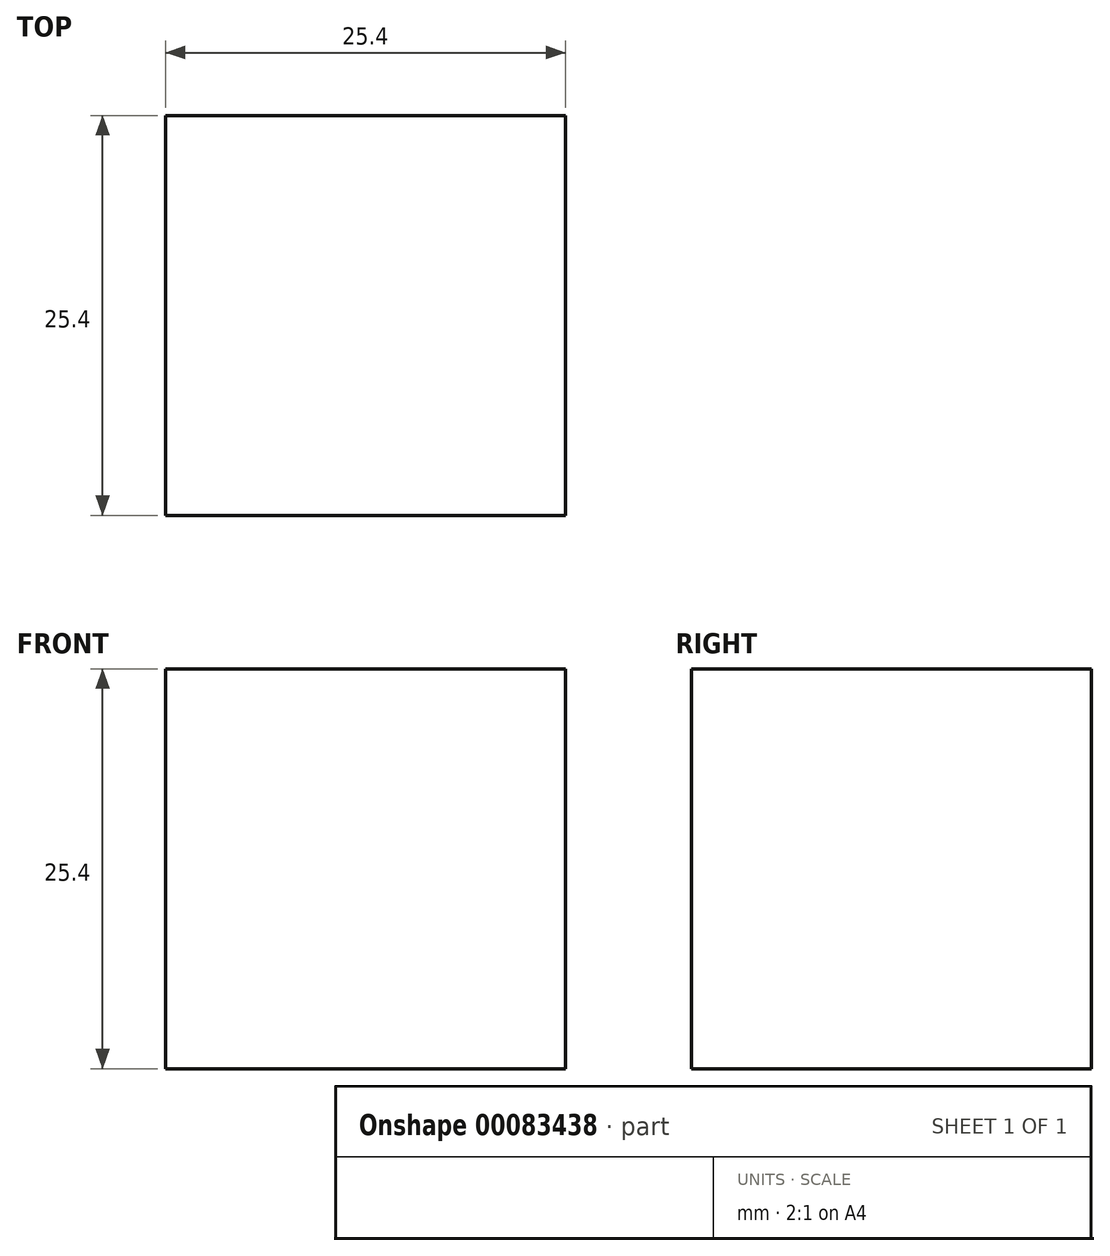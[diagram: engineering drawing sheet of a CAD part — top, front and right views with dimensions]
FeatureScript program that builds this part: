
annotation { "Feature Type Name" : "Feature", "Feature Type Description" : "" }
export const myFeature = defineFeature(function(context is Context, id is Id, definition is map)
    precondition{}
    {
        {
            var Q0;
            Q0=qCreatedBy(makeId("Top.planeOp"),FACE);
            var sketch = newSketch(context, id + "F0", { "sketchPlane" : qUnion([Q0])});
            skLineSegment(sketch, "E0.bottom", {"start": v(-12.7, 12.7) * mm, "end": v(12.7, 12.7) * mm});
            skLineSegment(sketch, "E0.top", {"start": v(-12.7, -12.7) * mm, "end": v(12.7, -12.7) * mm});
            skLineSegment(sketch, "E0.left", {"start": v(-12.7, 12.7) * mm, "end": v(-12.7, -12.7) * mm});
            skLineSegment(sketch, "E0.right", {"start": v(12.7, 12.7) * mm, "end": v(12.7, -12.7) * mm});
            skPoint(sketch, "E0.middle", {"position": v(0, 0) * mm});
            skSolve(sketch);
        }
        {
            var Q0;
            Q0 = qSketchRegion(id + "F0", true);
            extrude(context, id + "F1", {"entities" : qUnion([Q0]), "depth" : 25.4 * mm});
        }
    });
